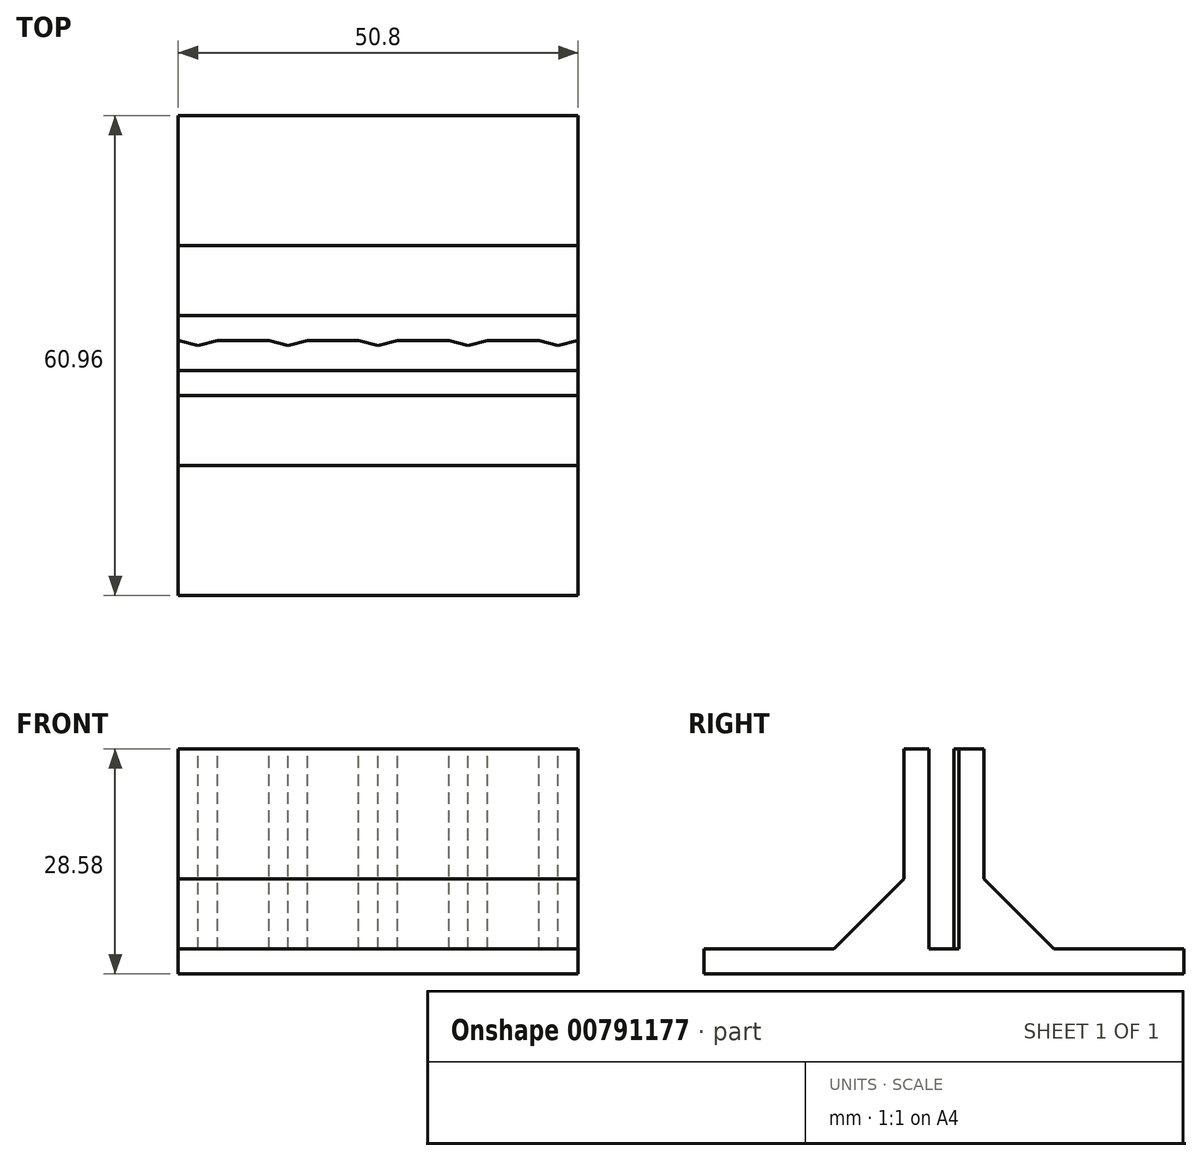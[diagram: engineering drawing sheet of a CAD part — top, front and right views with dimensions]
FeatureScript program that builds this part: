
annotation { "Feature Type Name" : "Feature", "Feature Type Description" : "" }
export const myFeature = defineFeature(function(context is Context, id is Id, definition is map)
    precondition{}
    {
        {
            var Q0;
            Q0=qCreatedBy(makeId("Right.planeOp"),FACE);
            var sketch = newSketch(context, id + "F0", { "sketchPlane" : qUnion([Q0])});
            skLineSegment(sketch, "E0", {"start": v(0, 0) * mm, "end": v(-30.48, 0) * mm});
            skLineSegment(sketch, "E1", {"start": v(-30.48, 0) * mm, "end": v(-30.48, 3.17) * mm});
            skLineSegment(sketch, "E2", {"start": v(-30.48, 3.17) * mm, "end": v(-5.08, 3.17) * mm});
            skLineSegment(sketch, "E3", {"start": v(-5.08, 3.17) * mm, "end": v(-5.08, 28.57) * mm});
            skLineSegment(sketch, "E4", {"start": v(-5.08, 28.58) * mm, "end": v(-1.9, 28.58) * mm});
            skLineSegment(sketch, "E5", {"start": v(-1.9, 28.57) * mm, "end": v(-1.9, 3.17) * mm});
            skLineSegment(sketch, "E6", {"start": v(-1.9, 3.17) * mm, "end": v(0, 3.17) * mm});
            skLineSegment(sketch, "E7.MirrorCS", {"start": v(1.9, 3.17) * mm, "end": v(0, 3.17) * mm});
            skLineSegment(sketch, "E8.MirrorCS", {"start": v(1.9, 28.57) * mm, "end": v(1.9, 3.17) * mm});
            skLineSegment(sketch, "E9.MirrorCS", {"start": v(5.08, 28.58) * mm, "end": v(1.9, 28.58) * mm});
            skLineSegment(sketch, "E10.MirrorCS", {"start": v(5.08, 3.17) * mm, "end": v(5.08, 28.57) * mm});
            skLineSegment(sketch, "E11.MirrorCS", {"start": v(30.48, 3.17) * mm, "end": v(5.08, 3.17) * mm});
            skLineSegment(sketch, "E12.MirrorCS", {"start": v(30.48, 0) * mm, "end": v(30.48, 3.17) * mm});
            skLineSegment(sketch, "E13.MirrorCS", {"start": v(0, 0) * mm, "end": v(30.48, 0) * mm});
            skSolve(sketch);
        }
        {
            var Q0;
            Q0=makeQuery(id+"F0.imprint","IMPRINT",FACE,{"disambiguationData":[TD([[makeQuery(id+"F0.imprint","IMPRINT",EDGE,{"derivedFrom":sQuery(id+"F0.wireOp",EDGE,"E0")}),-1.0]])]});
            extrude(context, id + "F1", {"entities" : qUnion([Q0]), "depth" : 50.8 * mm, "offsetDistance" : 25.4 * mm});
        }
        {
            var Q0;
            Q0=makeQuery(id+"F1.opExtrude","SWEPT_EDGE",EDGE,{"disambiguationData":[OSD([sQuery(id+"F0.wireOp",EDGE,"E10.MirrorCS"),sQuery(id+"F0.wireOp",EDGE,"E11.MirrorCS")])]});
            var Q1;
            Q1=makeQuery(id+"F1.opExtrude","SWEPT_EDGE",EDGE,{"disambiguationData":[OSD([sQuery(id+"F0.wireOp",EDGE,"E2"),sQuery(id+"F0.wireOp",EDGE,"E3")])]});
            chamfer(context, id + "F2", {"entities" : qUnion([Q0, Q1]), "width" : 8.9 * mm, "tangentPropagation" : true});
        }
        {
            var Q0;
            Q0=makeQuery(id+"F1.opExtrude","SWEPT_FACE",FACE,{"disambiguationData":[OSD([sQuery(id+"F0.wireOp",EDGE,"E9.MirrorCS")])]});
            var sketch = newSketch(context, id + "F3", { "sketchPlane" : qUnion([Q0])});
            skLineSegment(sketch, "E14", {"start": v(25.4, 1.9) * mm, "end": v(25.4, 1.27) * mm});
            skLineSegment(sketch, "E15", {"start": v(25.4, 1.27) * mm, "end": v(27.86, 1.9) * mm});
            skLineSegment(sketch, "E16", {"start": v(25.4, 1.27) * mm, "end": v(22.94, 1.9) * mm});
            skLineSegment(sketch, "E17.1.0.0", {"start": v(36.83, 1.27) * mm, "end": v(39.29, 1.9) * mm});
            skLineSegment(sketch, "E17.1.0.1", {"start": v(36.83, 1.27) * mm, "end": v(34.37, 1.9) * mm});
            skLineSegment(sketch, "E17.2.0.0", {"start": v(48.26, 1.27) * mm, "end": v(50.72, 1.9) * mm});
            skLineSegment(sketch, "E17.2.0.1", {"start": v(48.26, 1.27) * mm, "end": v(45.8, 1.9) * mm});
            skLineSegment(sketch, "E17.direction1", {"start": v(25.4, 1.27) * mm, "end": v(36.83, 1.27) * mm, "construction": true});
            skLineSegment(sketch, "E18.1.0.0", {"start": v(13.97, 1.27) * mm, "end": v(11.51, 1.9) * mm});
            skLineSegment(sketch, "E18.1.0.1", {"start": v(13.97, 1.27) * mm, "end": v(16.43, 1.9) * mm});
            skLineSegment(sketch, "E18.2.0.0", {"start": v(2.54, 1.27) * mm, "end": v(0.08, 1.9) * mm});
            skLineSegment(sketch, "E18.2.0.1", {"start": v(2.54, 1.27) * mm, "end": v(5, 1.9) * mm});
            skLineSegment(sketch, "E18.2.0.2", {"start": v(13.97, 1.27) * mm, "end": v(16.43, 1.9) * mm});
            skLineSegment(sketch, "E18.direction1", {"start": v(22.94, 1.9) * mm, "end": v(11.51, 1.9) * mm, "construction": true});
            skSolve(sketch);
        }
        {
            var Q0;
            {var subQ0=sQuery(id+"F3.wireOp",EDGE,"E18.2.0.0");Q0=makeQuery(id+"F3.imprint","IMPRINT",FACE,{"disambiguationData":[TD([[makeQuery(id+"F3.imprint","IMPRINT",EDGE,{"derivedFrom":subQ0}),-1.0]])]});}
            var Q1;
            {var subQ0=sQuery(id+"F3.wireOp",EDGE,"E18.1.0.0");Q1=makeQuery(id+"F3.imprint","IMPRINT",FACE,{"disambiguationData":[TD([[makeQuery(id+"F3.imprint","IMPRINT",EDGE,{"derivedFrom":subQ0}),-1.0]])]});}
            var Q2;
            {var subQ0=sQuery(id+"F3.wireOp",EDGE,"E14");Q2=makeQuery(id+"F3.imprint","IMPRINT",FACE,{"disambiguationData":[TD([[makeQuery(id+"F3.imprint","IMPRINT",EDGE,{"derivedFrom":subQ0}),1.0]])]});}
            var Q3;
            {var subQ0=sQuery(id+"F3.wireOp",EDGE,"E14");Q3=makeQuery(id+"F3.imprint","IMPRINT",FACE,{"disambiguationData":[TD([[makeQuery(id+"F3.imprint","IMPRINT",EDGE,{"derivedFrom":subQ0}),-1.0]])]});}
            var Q4;
            {var subQ0=sQuery(id+"F3.wireOp",EDGE,"E17.1.0.0");Q4=makeQuery(id+"F3.imprint","IMPRINT",FACE,{"disambiguationData":[TD([[makeQuery(id+"F3.imprint","IMPRINT",EDGE,{"derivedFrom":subQ0}),1.0]])]});}
            var Q5;
            {var subQ0=sQuery(id+"F3.wireOp",EDGE,"E17.2.0.0");Q5=makeQuery(id+"F3.imprint","IMPRINT",FACE,{"disambiguationData":[TD([[makeQuery(id+"F3.imprint","IMPRINT",EDGE,{"derivedFrom":subQ0}),1.0]])]});}
            var Q6;
            Q6=makeQuery(id+"F1.opExtrude","SWEPT_FACE",FACE,{"disambiguationData":[OSD([sQuery(id+"F0.wireOp",EDGE,"E6"),sQuery(id+"F0.wireOp",EDGE,"E7.MirrorCS")])]});
            extrude(context, id + "F4", {"entities" : qUnion([Q0, Q1, Q2, Q3, Q4, Q5]), "operationType" : NewBodyOperationType.ADD, "endBound" : BoundingType.UP_TO_SURFACE, "oppositeDirection" : true, "depth" : 25.4 * mm, "endBoundEntityFace" : qUnion([Q6]), "offsetDistance" : 25.4 * mm});
        }
    });
